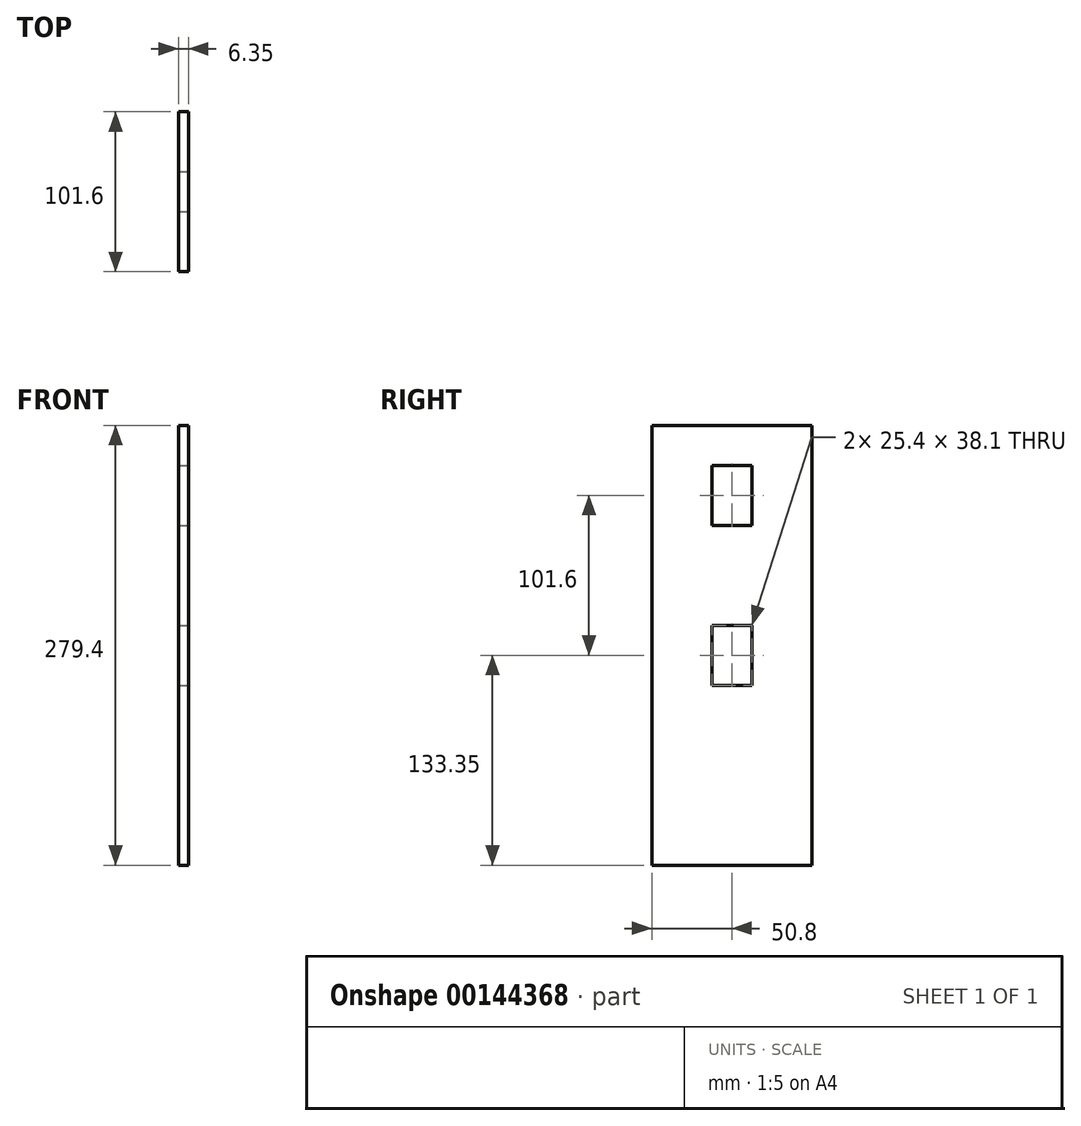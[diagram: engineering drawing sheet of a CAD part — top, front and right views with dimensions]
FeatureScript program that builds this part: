
annotation { "Feature Type Name" : "Feature", "Feature Type Description" : "" }
export const myFeature = defineFeature(function(context is Context, id is Id, definition is map)
    precondition{}
    {
        {
            var Q0;
            Q0=qCreatedBy(makeId("Right.planeOp"),FACE);
            var sketch = newSketch(context, id + "F0", { "sketchPlane" : qUnion([Q0])});
            skLineSegment(sketch, "E0.bottom", {"start": v(0, 0) * mm, "end": v(101.6, 0) * mm});
            skLineSegment(sketch, "E0.top", {"start": v(0, 279.4) * mm, "end": v(101.6, 279.4) * mm});
            skLineSegment(sketch, "E0.left", {"start": v(0, 0) * mm, "end": v(0, 279.4) * mm});
            skLineSegment(sketch, "E0.right", {"start": v(101.6, 0) * mm, "end": v(101.6, 279.4) * mm});
            skSolve(sketch);
        }
        {
            var Q0;
            Q0=makeQuery(id+"F0.imprint","IMPRINT",FACE,{"disambiguationData":[TD([[makeQuery(id+"F0.imprint","IMPRINT",EDGE,{"derivedFrom":sQuery(id+"F0.wireOp",EDGE,"E0.bottom")}),1.0]])]});
            extrude(context, id + "F1", {"entities" : qUnion([Q0]), "depth" : 6.35 * mm});
        }
        {
            var Q0;
            Q0=makeQuery(id+"F1.opExtrude","CAP_FACE",FACE,{"disambiguationData":[OSD([sQuery(id+"F0.wireOp",EDGE,"E0.bottom"),sQuery(id+"F0.wireOp",EDGE,"E0.top"),sQuery(id+"F0.wireOp",EDGE,"E0.left"),sQuery(id+"F0.wireOp",EDGE,"E0.right")])],"isStart":false});
            var sketch = newSketch(context, id + "F2", { "sketchPlane" : qUnion([Q0])});
            skLineSegment(sketch, "E1.bottom", {"start": v(38.1, 254) * mm, "end": v(63.5, 254) * mm});
            skLineSegment(sketch, "E1.top", {"start": v(38.1, 215.9) * mm, "end": v(63.5, 215.9) * mm});
            skLineSegment(sketch, "E1.left", {"start": v(38.1, 254) * mm, "end": v(38.1, 215.9) * mm});
            skLineSegment(sketch, "E1.right", {"start": v(63.5, 254) * mm, "end": v(63.5, 215.9) * mm});
            skLineSegment(sketch, "E2.bottom", {"start": v(38.1, 152.4) * mm, "end": v(63.5, 152.4) * mm});
            skLineSegment(sketch, "E2.top", {"start": v(38.1, 114.3) * mm, "end": v(63.5, 114.3) * mm});
            skLineSegment(sketch, "E2.left", {"start": v(38.1, 152.4) * mm, "end": v(38.1, 114.3) * mm});
            skLineSegment(sketch, "E2.right", {"start": v(63.5, 152.4) * mm, "end": v(63.5, 114.3) * mm});
            skLineSegment(sketch, "E3", {"start": v(50.8, 279.4) * mm, "end": v(50.8, 254) * mm, "construction": true});
            skSolve(sketch);
        }
        {
            var Q0;
            Q0 = qSketchRegion(id + "F2", true);
            extrude(context, id + "F3", {"entities" : qUnion([Q0]), "operationType" : NewBodyOperationType.REMOVE, "oppositeDirection" : true, "depth" : 6.35 * mm});
        }
    });
